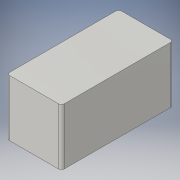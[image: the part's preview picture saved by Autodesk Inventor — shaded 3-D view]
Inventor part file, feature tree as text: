
AUTODESK INVENTOR PART (.ipt)
format: ipt  version: 2016 (Build 200138000, 138)  size: 92,160 bytes
history: native  units: mm
features: other x1, extrude x1, fillet x1, sketch x1
ambient origin geometry x8: Origin, YZ Plane, XZ Plane, XY Plane, X Axis, Y Axis, Z Axis, Center Point
bodies: Body1 (feature_tree)
feature tree (4):
  other  "Sólido1"
  extrude  "Extrusión1"  Depth=40.6mm
  fillet  "Empalme1"  Radius=20.5mm
  sketch  "Boceto1"  dims[d0=19.8mm d1=40.6mm d2=20.5mm d3=0.0mm d4=1.0mm]
